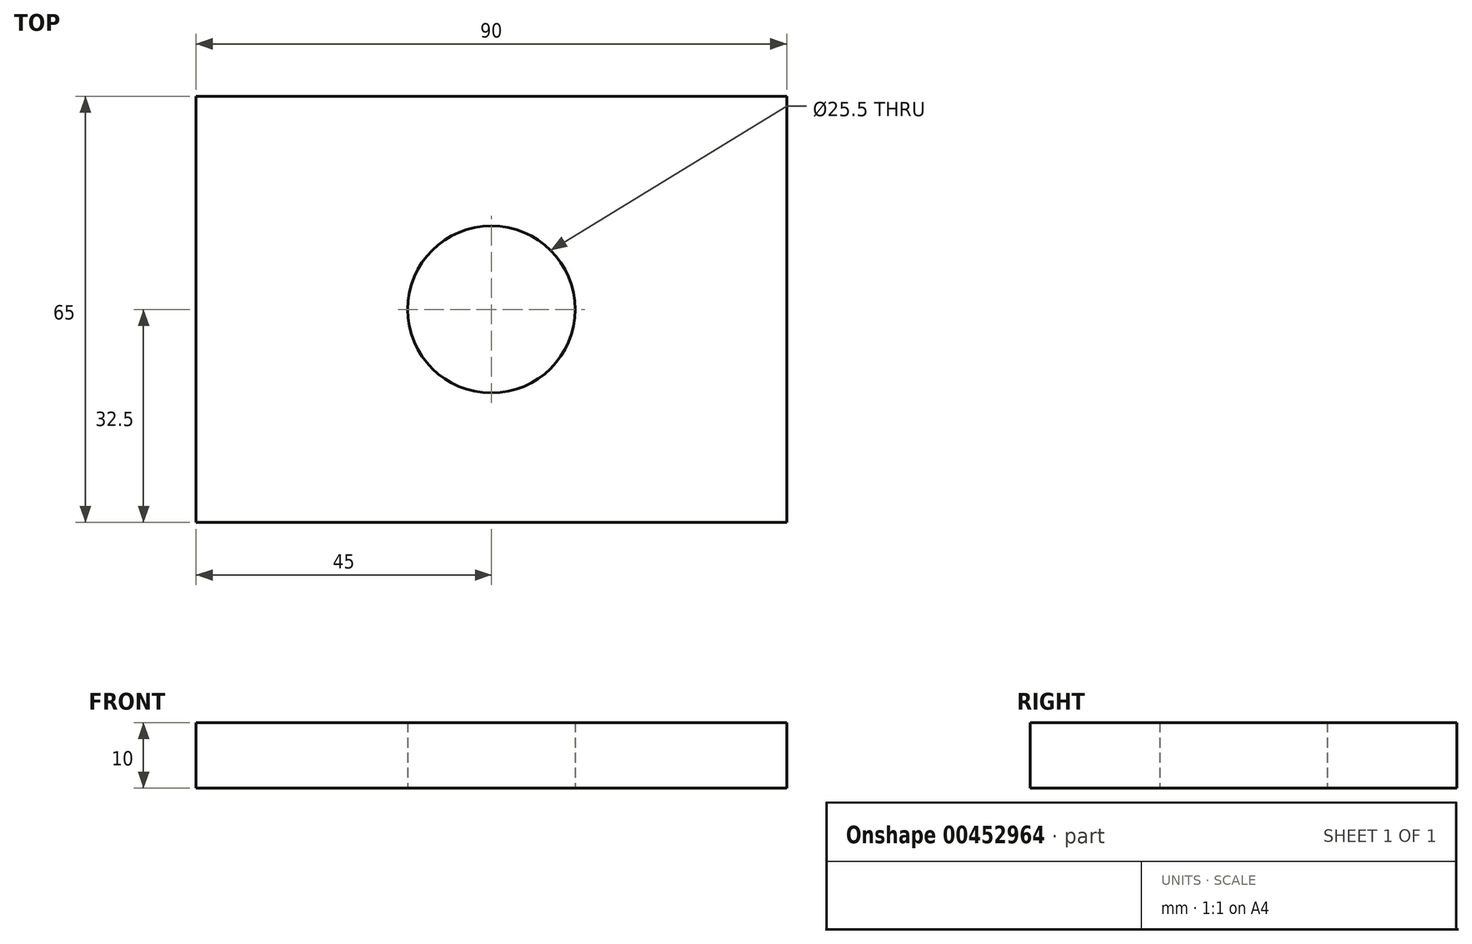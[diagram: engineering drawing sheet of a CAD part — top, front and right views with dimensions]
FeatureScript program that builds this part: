
annotation { "Feature Type Name" : "Feature", "Feature Type Description" : "" }
export const myFeature = defineFeature(function(context is Context, id is Id, definition is map)
    precondition{}
    {
        {
            var Q0;
            Q0=qCreatedBy(makeId("Top.planeOp"),FACE);
            var sketch = newSketch(context, id + "F0", { "sketchPlane" : qUnion([Q0])});
            skLineSegment(sketch, "E0.bottom", {"start": v(-45, 32.5) * mm, "end": v(45, 32.5) * mm});
            skLineSegment(sketch, "E0.top", {"start": v(-45, -32.5) * mm, "end": v(45, -32.5) * mm});
            skLineSegment(sketch, "E0.left", {"start": v(-45, 32.5) * mm, "end": v(-45, -32.5) * mm});
            skLineSegment(sketch, "E0.right", {"start": v(45, 32.5) * mm, "end": v(45, -32.5) * mm});
            skCircle(sketch, "E1", {"center": v(0, 0) * mm, "radius": 12.75 * mm});
            skSolve(sketch);
        }
        {
            var Q0;
            Q0 = qSketchRegion(id + "F0", true);
            extrude(context, id + "F1", {"entities" : qUnion([Q0]), "depth" : 10 * mm});
        }
    });
